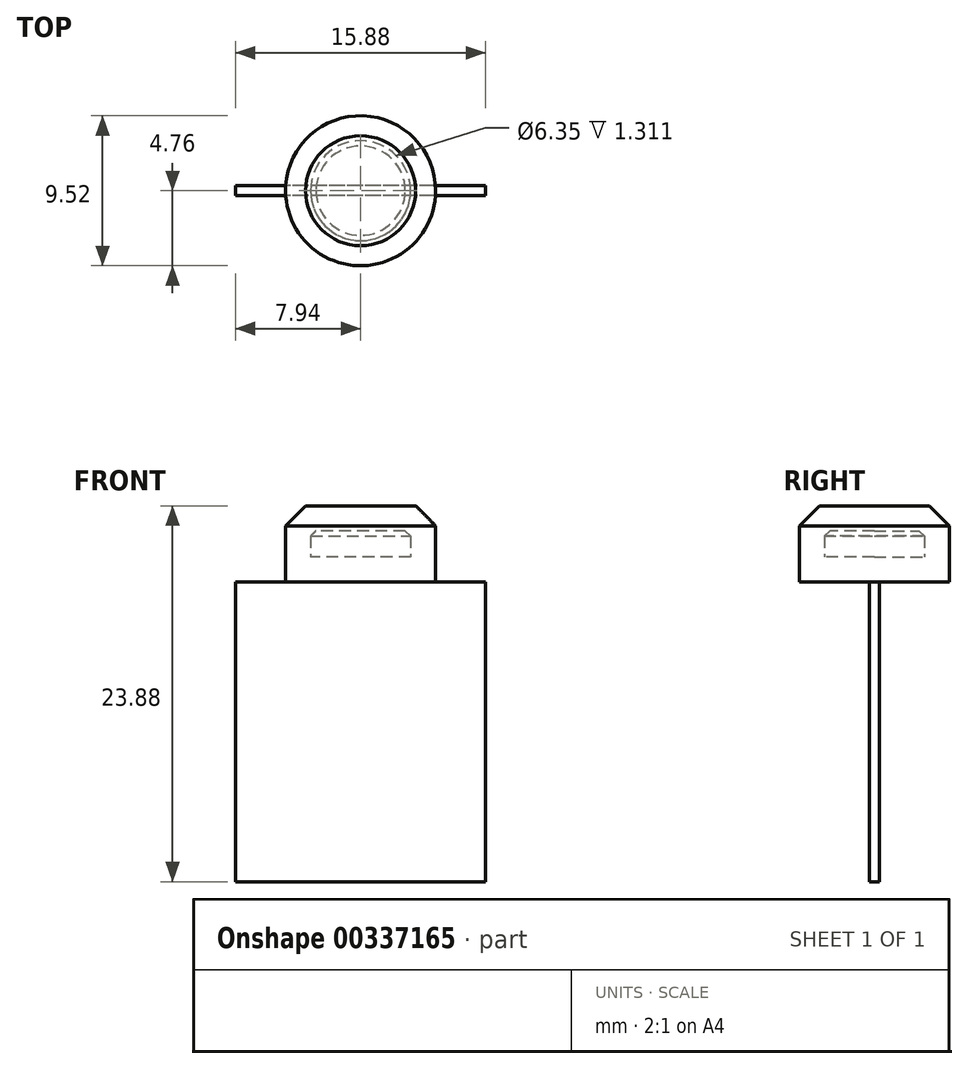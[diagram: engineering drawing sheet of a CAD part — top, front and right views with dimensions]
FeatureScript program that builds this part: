
annotation { "Feature Type Name" : "Feature", "Feature Type Description" : "" }
export const myFeature = defineFeature(function(context is Context, id is Id, definition is map)
    precondition{}
    {
        {
            assignVariable(context, id + "F0", {"name" : "W", "anyValue" : .625});
        }
        {
            var Q0;
            Q0=qCreatedBy(makeId("Front.planeOp"),FACE);
            var sketch = newSketch(context, id + "F1", { "sketchPlane" : qUnion([Q0])});
            skLineSegment(sketch, "E0.bottom", {"start": v(7.94, 9.53) * mm, "end": v(-7.94, 9.53) * mm});
            skLineSegment(sketch, "E0.top", {"start": v(7.94, -9.52) * mm, "end": v(-7.94, -9.52) * mm});
            skLineSegment(sketch, "E0.left", {"start": v(7.94, 9.53) * mm, "end": v(7.94, -9.52) * mm});
            skLineSegment(sketch, "E0.right", {"start": v(-7.94, 9.52) * mm, "end": v(-7.94, -9.52) * mm});
            skPoint(sketch, "E0.middle", {"position": v(0, 0) * mm});
            skSolve(sketch);
        }
        {
            var Q0;
            Q0=qSketchRegion(id+"F1",true);
            extrude(context, id + "F2", {"entities" : qUnion([Q0]), "depth" : (getVariable(context, 'W')) * mm, "symmetric" : true});
        }
        {
            var Q0;
            Q0=makeQuery(id+"F2.opExtrude","SWEPT_FACE",FACE,{"disambiguationData":[OSD([sQuery(id+"F1.wireOp",EDGE,"E0.bottom")])]});
            var sketch = newSketch(context, id + "F3", { "sketchPlane" : qUnion([Q0])});
            skCircle(sketch, "E1", {"center": v(0, 0) * mm, "radius": 4.76 * mm});
            skSolve(sketch);
        }
        {
            var Q0;
            Q0=qSketchRegion(id+"F3",true);
            extrude(context, id + "F4", {"entities" : qUnion([Q0]), "operationType" : NewBodyOperationType.ADD, "depth" : 4.83 * mm});
        }
        {
            var Q0;
            Q0=makeQuery(id+"F4.opExtrude","CAP_EDGE",EDGE,{"disambiguationData":[OSD([sQuery(id+"F3.wireOp",EDGE,"E1")])],"isStart":false});
            chamfer(context, id + "F5", {"entities" : qUnion([Q0]), "width" : 1.27 * mm, "tangentPropagation" : true});
        }
        {
            var Q0;
            Q0=makeQuery(id+"F2.opExtrude","SWEPT_FACE",FACE,{"disambiguationData":[OSD([sQuery(id+"F1.wireOp",EDGE,"E0.top")])]});
            shell(context, id + "F6", {"entities" : qUnion([Q0]), "thickness" : 1.59 * mm});
        }
    });
